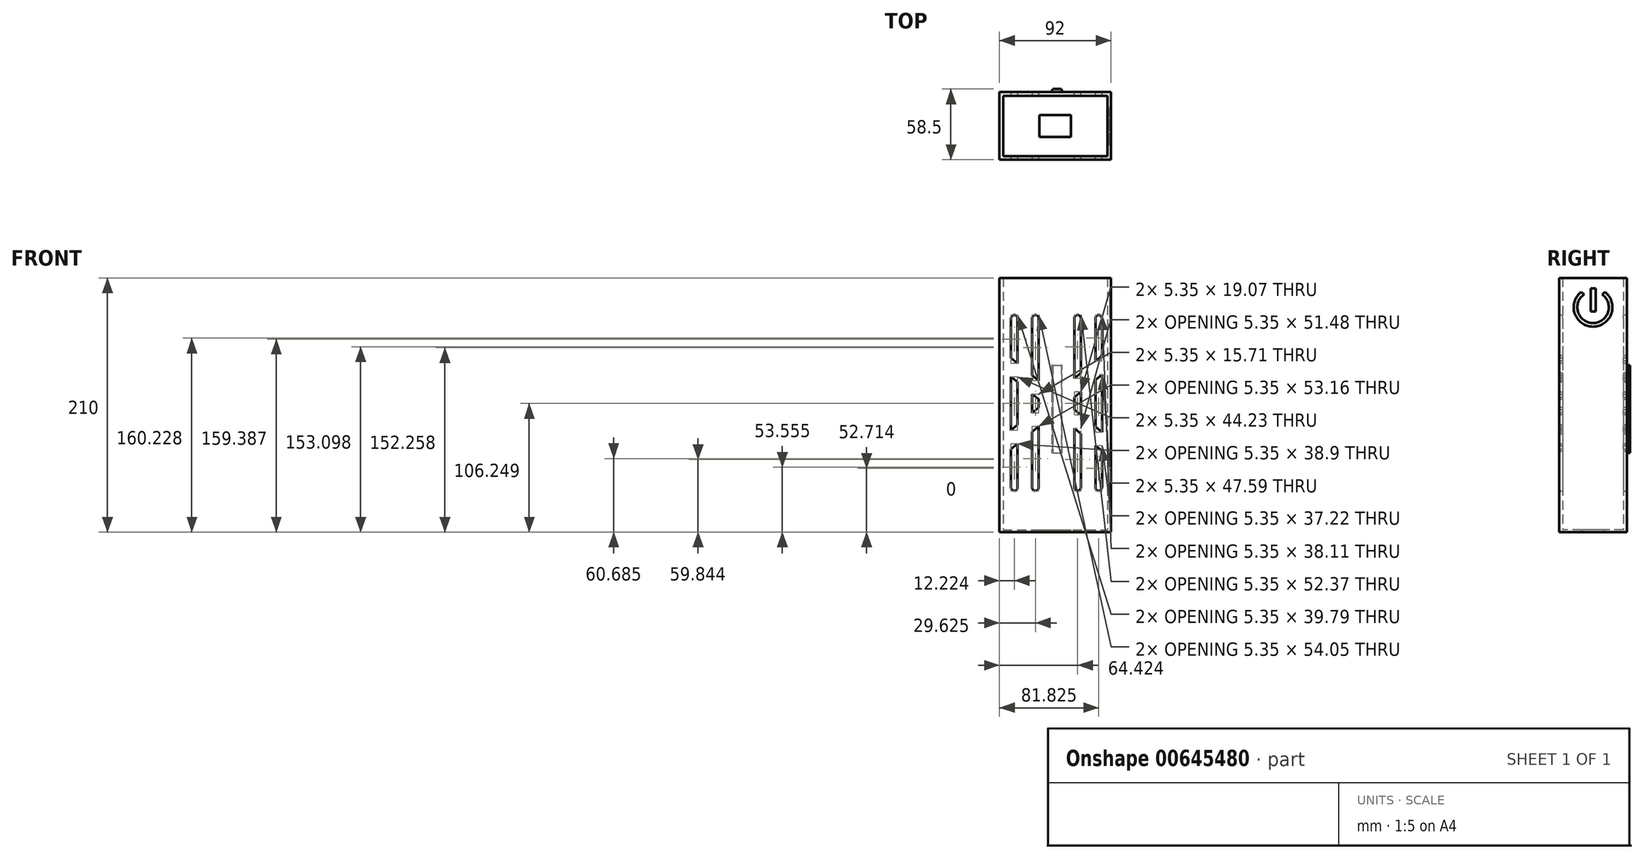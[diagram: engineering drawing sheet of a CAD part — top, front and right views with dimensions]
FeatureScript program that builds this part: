
annotation { "Feature Type Name" : "Feature", "Feature Type Description" : "" }
export const myFeature = defineFeature(function(context is Context, id is Id, definition is map)
    precondition{}
    {
        {
            var Q0;
            Q0=qCreatedBy(makeId("Top.planeOp"),FACE);
            var sketch = newSketch(context, id + "F0", { "sketchPlane" : qUnion([Q0])});
            skLineSegment(sketch, "E0.bottom", {"start": v(-38.14, 33.96) * mm, "end": v(53.86, 33.96) * mm});
            skLineSegment(sketch, "E0.top", {"start": v(-38.14, -22.04) * mm, "end": v(53.86, -22.04) * mm});
            skLineSegment(sketch, "E0.left", {"start": v(-38.14, 33.96) * mm, "end": v(-38.14, -22.04) * mm});
            skLineSegment(sketch, "E0.right", {"start": v(53.86, 33.96) * mm, "end": v(53.86, -22.04) * mm});
            skLineSegment(sketch, "E1.bottom", {"start": v(-35.14, 30.96) * mm, "end": v(50.86, 30.96) * mm});
            skLineSegment(sketch, "E1.top", {"start": v(-35.14, -19.04) * mm, "end": v(50.86, -19.04) * mm});
            skLineSegment(sketch, "E1.left", {"start": v(-35.14, 30.96) * mm, "end": v(-35.14, -19.04) * mm});
            skLineSegment(sketch, "E1.right", {"start": v(50.86, 30.96) * mm, "end": v(50.86, -19.04) * mm});
            skSolve(sketch);
        }
        {
            var Q0;
            Q0=makeQuery(id+"F0.imprint","IMPRINT",FACE,{"disambiguationData":[TD([[makeQuery(id+"F0.imprint","IMPRINT",EDGE,{"derivedFrom":sQuery(id+"F0.wireOp",EDGE,"E0.bottom")}),-1.0]])]});
            extrude(context, id + "F1", {"entities" : qUnion([Q0]), "depth" : 210 * mm, "offsetDistance" : 25 * mm});
        }
        {
            var Q0;
            Q0=qCreatedBy(makeId("Top.planeOp"),FACE);
            var sketch = newSketch(context, id + "F2", { "sketchPlane" : qUnion([Q0])});
            skLineSegment(sketch, "E2.bottom", {"start": v(-35.14, 30.96) * mm, "end": v(50.86, 30.96) * mm});
            skLineSegment(sketch, "E2.top", {"start": v(-35.14, -19.04) * mm, "end": v(50.86, -19.04) * mm});
            skLineSegment(sketch, "E2.left", {"start": v(-35.14, 30.96) * mm, "end": v(-35.14, -19.04) * mm});
            skLineSegment(sketch, "E2.right", {"start": v(50.86, 30.96) * mm, "end": v(50.86, -19.04) * mm});
            skSolve(sketch);
        }
        {
            var Q0;
            Q0=makeQuery(id+"F2.imprint","IMPRINT",FACE,{"disambiguationData":[TD([[makeQuery(id+"F2.imprint","IMPRINT",EDGE,{"derivedFrom":sQuery(id+"F2.wireOp",EDGE,"E2.bottom")}),-1.0]])]});
            extrude(context, id + "F3", {"entities" : qUnion([Q0]), "operationType" : NewBodyOperationType.ADD, "depth" : 2 * mm, "offsetDistance" : 25 * mm});
        }
        {
            var Q0;
            Q0=makeQuery(id+"F3.opExtrude","CAP_FACE",FACE,{"disambiguationData":[OSD([sQuery(id+"F2.wireOp",EDGE,"E2.bottom"),sQuery(id+"F2.wireOp",EDGE,"E2.top"),sQuery(id+"F2.wireOp",EDGE,"E2.left"),sQuery(id+"F2.wireOp",EDGE,"E2.right")])],"isStart":false});
            var sketch = newSketch(context, id + "F4", { "sketchPlane" : qUnion([Q0])});
            skLineSegment(sketch, "E3.bottom", {"start": v(-5.14, 14.96) * mm, "end": v(20.86, 14.96) * mm});
            skLineSegment(sketch, "E3.top", {"start": v(-5.14, -3.04) * mm, "end": v(20.86, -3.04) * mm});
            skLineSegment(sketch, "E3.left", {"start": v(-5.14, 14.96) * mm, "end": v(-5.14, -3.04) * mm});
            skLineSegment(sketch, "E3.right", {"start": v(20.86, 14.96) * mm, "end": v(20.86, -3.04) * mm});
            skSolve(sketch);
        }
        {
            var Q0;
            Q0=makeQuery(id+"F4.imprint","IMPRINT",FACE,{"disambiguationData":[TD([[makeQuery(id+"F4.imprint","IMPRINT",EDGE,{"derivedFrom":sQuery(id+"F4.wireOp",EDGE,"E3.bottom")}),-1.0]])]});
            extrude(context, id + "F5", {"entities" : qUnion([Q0]), "operationType" : NewBodyOperationType.REMOVE, "oppositeDirection" : true, "depth" : 25 * mm, "offsetDistance" : 25 * mm});
        }
        {
            var Q0;
            Q0=makeQuery(id+"F3.boolean.opBoolean","MERGE",FACE,{"derivedFrom":[makeQuery(id+"F1.opExtrude","CAP_FACE",FACE,{"disambiguationData":[OSD([sQuery(id+"F0.wireOp",EDGE,"E0.bottom"),sQuery(id+"F0.wireOp",EDGE,"E0.top"),sQuery(id+"F0.wireOp",EDGE,"E0.left"),sQuery(id+"F0.wireOp",EDGE,"E0.right"),sQuery(id+"F0.wireOp",EDGE,"E1.bottom"),sQuery(id+"F0.wireOp",EDGE,"E1.top"),sQuery(id+"F0.wireOp",EDGE,"E1.left"),sQuery(id+"F0.wireOp",EDGE,"E1.right")])],"isStart":true}),makeQuery(id+"F3.opExtrude","CAP_FACE",FACE,{"disambiguationData":[OSD([sQuery(id+"F2.wireOp",EDGE,"E2.bottom"),sQuery(id+"F2.wireOp",EDGE,"E2.top"),sQuery(id+"F2.wireOp",EDGE,"E2.left"),sQuery(id+"F2.wireOp",EDGE,"E2.right")])],"isStart":true})]});
            var sketch = newSketch(context, id + "F6", { "sketchPlane" : qUnion([Q0])});
            skLineSegment(sketch, "E4", {"start": v(5.86, -33.96) * mm, "end": v(3.36, -36.46) * mm});
            skLineSegment(sketch, "E5", {"start": v(3.36, -36.46) * mm, "end": v(15.36, -36.46) * mm});
            skLineSegment(sketch, "E6", {"start": v(15.36, -36.46) * mm, "end": v(12.86, -33.96) * mm});
            skSolve(sketch);
        }
        {
            var Q0;
            {var subQ0=sQuery(id+"F6.wireOp",EDGE,"E4");Q0=makeQuery(id+"F6.imprint","IMPRINT",FACE,{"disambiguationData":[TD([[makeQuery(id+"F6.imprint","IMPRINT",EDGE,{"derivedFrom":subQ0}),1.0]])]});}
            extrude(context, id + "F7", {"entities" : qUnion([Q0]), "operationType" : NewBodyOperationType.ADD, "oppositeDirection" : true, "depth" : 137.7 * mm, "offsetDistance" : 25 * mm, "hasSecondDirection" : true, "secondDirectionOppositeDirection" : true, "secondDirectionDepth" : 65.3 * mm});
        }
        {
            var Q0;
            Q0=makeQuery(id+"F7.opExtrude","SWEPT_EDGE",EDGE,{"disambiguationData":[OSD([sQuery(id+"F6.wireOp",EDGE,"E5"),sQuery(id+"F6.wireOp",EDGE,"E6")])]});
            var Q1;
            Q1=makeQuery(id+"F7.opExtrude","SWEPT_EDGE",EDGE,{"disambiguationData":[OSD([sQuery(id+"F6.wireOp",EDGE,"E4"),sQuery(id+"F6.wireOp",EDGE,"E5")])]});
            chamfer(context, id + "F8", {"entities" : qUnion([Q0, Q1]), "width" : 1 * mm, "tangentPropagation" : true});
        }
        {
            var Q0;
            Q0=makeQuery(id+"F1.opExtrude","SWEPT_FACE",FACE,{"disambiguationData":[OSD([sQuery(id+"F0.wireOp",EDGE,"E0.bottom")])]});
            var sketch = newSketch(context, id + "F9", { "sketchPlane" : qUnion([Q0])});
            skLineSegment(sketch, "E7.left", {"start": v(-46.36, 176.6) * mm, "end": v(-46.36, 36.78) * mm});
            skLineSegment(sketch, "E7.right", {"start": v(-41.01, 176.6) * mm, "end": v(-41.01, 36.78) * mm});
            skArc(sketch, "E8", {"start": v(-41.01, 176.6) * mm, "mid": v(-43.68, 179.28) * mm, "end": v(-46.36, 176.6) * mm});
            skArc(sketch, "E9", {"start": v(-46.36, 36.78) * mm, "mid": v(-43.68, 34.1) * mm, "end": v(-41.01, 36.78) * mm});
            skArc(sketch, "E10.1.0.0", {"start": v(-23.61, 176.6) * mm, "mid": v(-26.28, 179.28) * mm, "end": v(-28.96, 176.6) * mm});
            skLineSegment(sketch, "E10.1.0.1", {"start": v(-28.96, 176.6) * mm, "end": v(-28.96, 36.78) * mm});
            skArc(sketch, "E10.1.0.2", {"start": v(-28.96, 36.78) * mm, "mid": v(-26.28, 34.1) * mm, "end": v(-23.61, 36.78) * mm});
            skLineSegment(sketch, "E10.1.0.3", {"start": v(-23.61, 176.6) * mm, "end": v(-23.61, 36.78) * mm});
            skArc(sketch, "E10.2.0.0", {"start": v(-6.21, 176.6) * mm, "mid": v(-8.88, 179.28) * mm, "end": v(-11.56, 176.6) * mm});
            skLineSegment(sketch, "E10.2.0.1", {"start": v(-11.56, 176.6) * mm, "end": v(-11.56, 36.78) * mm});
            skArc(sketch, "E10.2.0.2", {"start": v(-11.56, 36.78) * mm, "mid": v(-8.88, 34.1) * mm, "end": v(-6.21, 36.78) * mm});
            skLineSegment(sketch, "E10.2.0.3", {"start": v(-6.21, 176.6) * mm, "end": v(-6.21, 36.78) * mm});
            skArc(sketch, "E10.3.0.0", {"start": v(11.19, 176.6) * mm, "mid": v(8.52, 179.28) * mm, "end": v(5.84, 176.6) * mm});
            skLineSegment(sketch, "E10.3.0.1", {"start": v(5.84, 176.6) * mm, "end": v(5.84, 36.78) * mm});
            skArc(sketch, "E10.3.0.2", {"start": v(5.84, 36.78) * mm, "mid": v(8.52, 34.1) * mm, "end": v(11.19, 36.78) * mm});
            skLineSegment(sketch, "E10.3.0.3", {"start": v(11.19, 176.6) * mm, "end": v(11.19, 36.78) * mm});
            skArc(sketch, "E10.4.0.0", {"start": v(28.59, 176.6) * mm, "mid": v(25.92, 179.28) * mm, "end": v(23.24, 176.6) * mm});
            skLineSegment(sketch, "E10.4.0.1", {"start": v(23.24, 176.6) * mm, "end": v(23.24, 36.78) * mm});
            skArc(sketch, "E10.4.0.2", {"start": v(23.24, 36.78) * mm, "mid": v(25.92, 34.1) * mm, "end": v(28.59, 36.78) * mm});
            skLineSegment(sketch, "E10.4.0.3", {"start": v(28.59, 176.6) * mm, "end": v(28.59, 36.78) * mm});
            skLineSegment(sketch, "E10.direction1", {"start": v(-46.36, 176.6) * mm, "end": v(-28.96, 176.6) * mm, "construction": true});
            skSolve(sketch);
        }
        {
            var Q0;
            Q0=makeQuery(id+"F9.imprint","IMPRINT",FACE,{"disambiguationData":[TD([[makeQuery(id+"F9.imprint","IMPRINT",EDGE,{"derivedFrom":sQuery(id+"F9.wireOp",EDGE,"E10.1.0.0")}),1.0]])]});
            var Q1;
            Q1=makeQuery(id+"F9.imprint","IMPRINT",FACE,{"disambiguationData":[TD([[makeQuery(id+"F9.imprint","IMPRINT",EDGE,{"derivedFrom":sQuery(id+"F9.wireOp",EDGE,"E10.3.0.0")}),1.0]])]});
            var Q2;
            Q2=makeQuery(id+"F9.imprint","IMPRINT",FACE,{"disambiguationData":[TD([[makeQuery(id+"F9.imprint","IMPRINT",EDGE,{"derivedFrom":sQuery(id+"F9.wireOp",EDGE,"E10.4.0.0")}),1.0]])]});
            var Q3;
            Q3=makeQuery(id+"F9.imprint","IMPRINT",FACE,{"disambiguationData":[TD([[makeQuery(id+"F9.imprint","IMPRINT",EDGE,{"derivedFrom":sQuery(id+"F9.wireOp",EDGE,"E7.left")}),1.0]])]});
            extrude(context, id + "F10", {"entities" : qUnion([Q0, Q1, Q2, Q3]), "operationType" : NewBodyOperationType.REMOVE, "endBound" : BoundingType.THROUGH_ALL, "oppositeDirection" : true, "depth" : 25 * mm, "offsetDistance" : 25 * mm});
        }
        {
            var Q0;
            Q0=makeQuery(id+"F1.opExtrude","SWEPT_FACE",FACE,{"disambiguationData":[OSD([sQuery(id+"F0.wireOp",EDGE,"E0.top")])]});
            var sketch = newSketch(context, id + "F11", { "sketchPlane" : qUnion([Q0])});
            skLineSegment(sketch, "E11", {"start": v(-38.14, 136.2) * mm, "end": v(53.86, 60.8) * mm});
            skLineSegment(sketch, "E12", {"start": v(53.86, 60.8) * mm, "end": v(53.86, 76.3) * mm});
            skLineSegment(sketch, "E13", {"start": v(53.86, 76.3) * mm, "end": v(-38.14, 151.7) * mm});
            skLineSegment(sketch, "E14", {"start": v(-38.14, 151.7) * mm, "end": v(-38.14, 136.2) * mm});
            skLineSegment(sketch, "E15", {"start": v(-38.14, 60.8) * mm, "end": v(53.86, 136.2) * mm});
            skLineSegment(sketch, "E16", {"start": v(53.86, 136.2) * mm, "end": v(53.86, 151.7) * mm});
            skLineSegment(sketch, "E17", {"start": v(53.86, 151.7) * mm, "end": v(-38.14, 76.3) * mm});
            skLineSegment(sketch, "E18", {"start": v(-38.14, 76.3) * mm, "end": v(-38.14, 60.8) * mm});
            skSolve(sketch);
        }
        {
            var Q0;
            Q0 = qSketchRegion(id + "F11", true);
            extrude(context, id + "F12", {"entities" : qUnion([Q0]), "operationType" : NewBodyOperationType.ADD, "oppositeDirection" : true, "depth" : 3 * mm, "offsetDistance" : 25 * mm});
        }
        {
            var Q0;
            Q0 = qSketchRegion(id + "F11", true);
            extrude(context, id + "F13", {"entities" : qUnion([Q0]), "operationType" : NewBodyOperationType.ADD, "oppositeDirection" : true, "depth" : 56 * mm, "offsetDistance" : 25 * mm, "hasSecondDirection" : true, "secondDirectionOppositeDirection" : true, "secondDirectionDepth" : 53 * mm});
        }
        {
            var Q0;
            Q0=makeQuery(id+"F1.opExtrude","SWEPT_FACE",FACE,{"disambiguationData":[OSD([sQuery(id+"F0.wireOp",EDGE,"E0.right")])]});
            var sketch = newSketch(context, id + "F14", { "sketchPlane" : qUnion([Q0])});
            skArc(sketch, "E19", {"start": v(-3.79, 198.37) * mm, "mid": v(5.96, 169.68) * mm, "end": v(15.71, 198.37) * mm});
            skArc(sketch, "E20", {"start": v(-1.49, 196.33) * mm, "mid": v(5.96, 172.68) * mm, "end": v(13.41, 196.33) * mm});
            skLineSegment(sketch, "E21", {"start": v(-1.49, 196.33) * mm, "end": v(-3.79, 198.37) * mm});
            skLineSegment(sketch, "E22", {"start": v(13.41, 196.33) * mm, "end": v(15.71, 198.37) * mm});
            skLineSegment(sketch, "E23.bottom", {"start": v(4.03, 201.35) * mm, "end": v(8.03, 201.35) * mm});
            skLineSegment(sketch, "E23.top", {"start": v(4.03, 182.23) * mm, "end": v(8.03, 182.23) * mm});
            skLineSegment(sketch, "E23.left", {"start": v(4.03, 201.35) * mm, "end": v(4.03, 182.23) * mm});
            skLineSegment(sketch, "E23.right", {"start": v(8.03, 201.35) * mm, "end": v(8.03, 182.23) * mm});
            skSolve(sketch);
        }
        {
            var Q0;
            Q0 = qSketchRegion(id + "F14", true);
            extrude(context, id + "F15", {"entities" : qUnion([Q0]), "operationType" : NewBodyOperationType.REMOVE, "oppositeDirection" : true, "depth" : 1 * mm, "offsetDistance" : 25 * mm});
        }
    });
